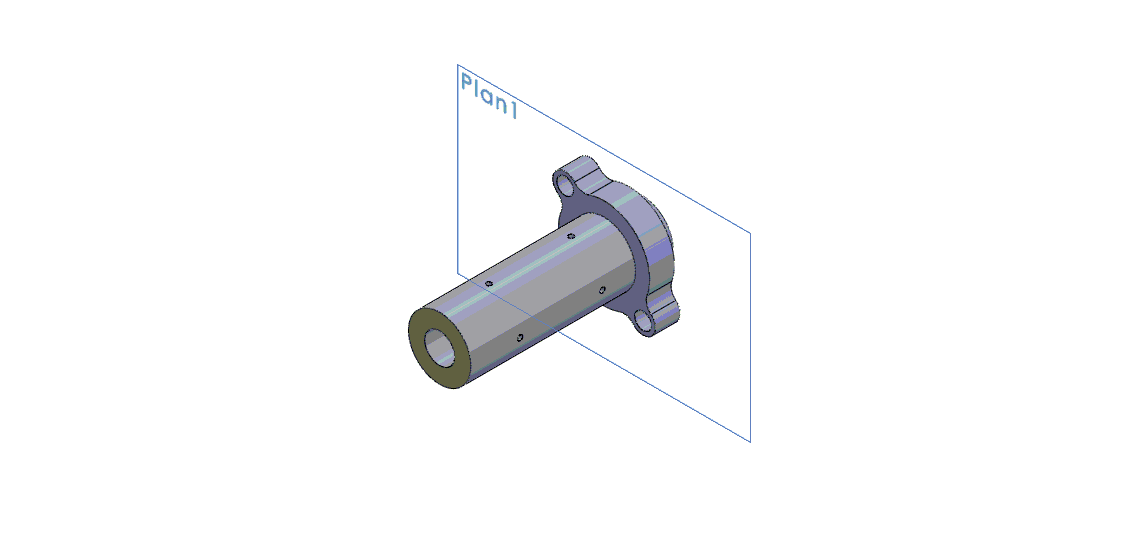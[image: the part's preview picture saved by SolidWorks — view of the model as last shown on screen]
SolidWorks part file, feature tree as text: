
SOLIDWORKS PART (.sldprt)
format: sldprt  version: not decoded by parser v0  size: 219,136 bytes
history: native  units: mm
features: sketch x6, plane x4, cut_extrude x4, extrude x2, material x1 (+10 scaffold rows collapsed)
feature tree (27):
  scaffold x10  (default folders/planes/origin — collapsed)
  material  "Matériau <non spécifié>"
  plane  "FRONT"
  plane  "TOP"
  plane  "RIGHT"
  plane  "Plan1"  Offset=838.2mm
  sketch  "Esquisse1"  dims[D2=~3.520382mm D1=67.0mm]
  extrude  "Boss.-Extru.1"  Depth=15mm
  sketch  "Esquisse9"  dims[D1=~8.950813mm]
  extrude  "Boss.-Extru.4"  Depth=100mm
  sketch  "Esquisse12"  dims[D1=~6.616621mm]
  cut_extrude  "Enlèv. mat.-Extru.2"  [1 undecoded]
  sketch  "Esquisse13"  dims[D1=~4.891676mm]
  cut_extrude  "Enlèv. mat.-Extru.3"  Depth=7mm
  sketch  "Esquisse14"  dims[D1=20.0mm D2=50.0mm]
  cut_extrude  "Enlèv. mat.-Extru.4"  Depth=7mm
  sketch  "Esquisse15"  dims[D1=20.0mm D2=50.0mm]
  cut_extrude  "Enlèv. mat.-Extru.5"  Depth=7mm
decode coverage: 11 of 12 modeling features carry decoded parameters
note: ~ marks probable driven/reference dimensions
note: 1 parameter value undecoded
note: suppression state not decoded; provenance and decode notes live in map.json
